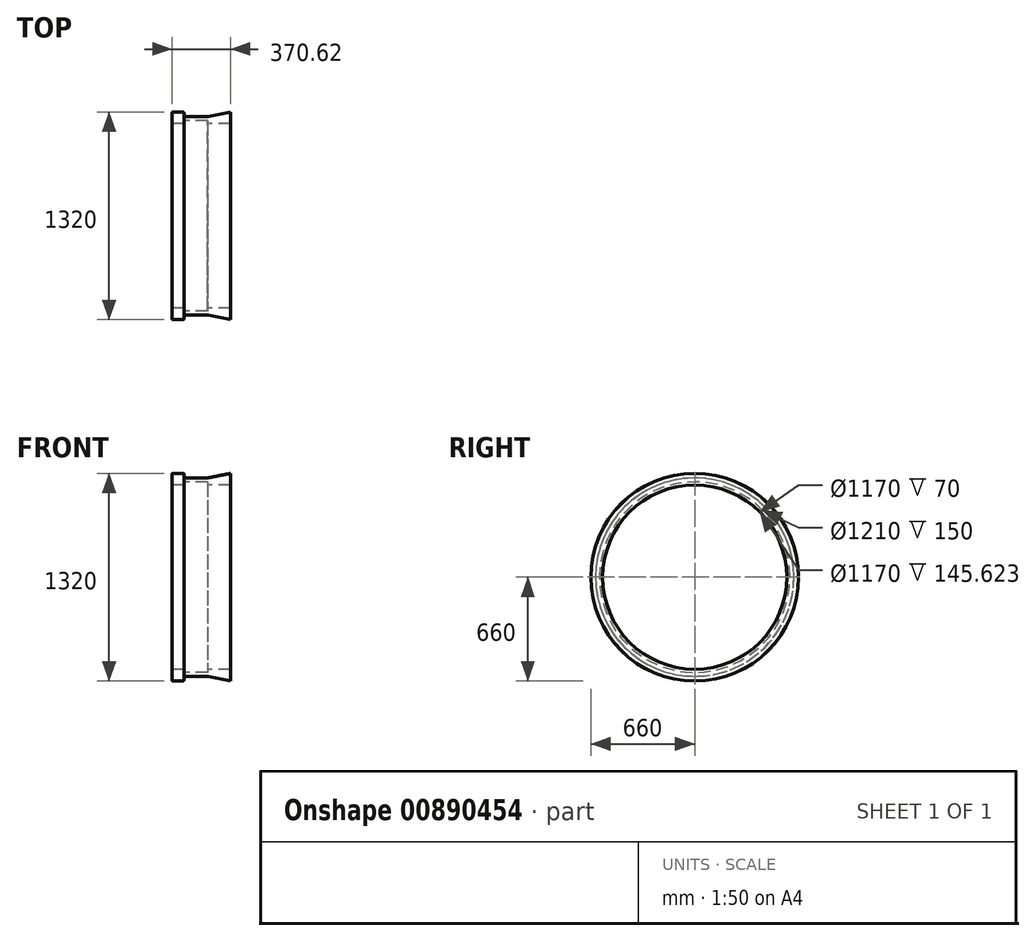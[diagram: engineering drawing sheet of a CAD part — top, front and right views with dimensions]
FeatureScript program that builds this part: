
annotation { "Feature Type Name" : "Feature", "Feature Type Description" : "" }
export const myFeature = defineFeature(function(context is Context, id is Id, definition is map)
    precondition{}
    {
        {
            var Q0;
            Q0=qCreatedBy(makeId("Front.planeOp"),FACE);
            var sketch = newSketch(context, id + "F0", { "sketchPlane" : qUnion([Q0])});
            skLineSegment(sketch, "E0", {"start": v(0, 660) * mm, "end": v(0, 585) * mm});
            skLineSegment(sketch, "E1", {"start": v(0, 0) * mm, "end": v(36.17, 0) * mm, "construction": true});
            skLineSegment(sketch, "E2", {"start": v(0, 585) * mm, "end": v(75, 585) * mm});
            skLineSegment(sketch, "E3", {"start": v(500, 685) * mm, "end": v(1070, 685) * mm});
            skLineSegment(sketch, "E4", {"start": v(1070, 685) * mm, "end": v(1070, 585) * mm});
            skLineSegment(sketch, "E5", {"start": v(0, 660) * mm, "end": v(75, 660) * mm});
            skLineSegment(sketch, "E6", {"start": v(75, 660) * mm, "end": v(75, 630) * mm});
            skLineSegment(sketch, "E7", {"start": v(75, 630) * mm, "end": v(75, 630) * mm});
            skLineSegment(sketch, "E8", {"start": v(75, 630) * mm, "end": v(225, 630) * mm});
            skLineSegment(sketch, "E9", {"start": v(225, 630) * mm, "end": v(225, 630) * mm});
            skLineSegment(sketch, "E10", {"start": v(500, 685) * mm, "end": v(225, 630) * mm});
            skLineSegment(sketch, "E11", {"start": v(75, 585) * mm, "end": v(75, 605) * mm});
            skLineSegment(sketch, "E12", {"start": v(75, 605) * mm, "end": v(225, 605) * mm});
            skLineSegment(sketch, "E13", {"start": v(225, 605) * mm, "end": v(225, 585) * mm});
            skLineSegment(sketch, "E14.trimOffspring", {"start": v(225, 585) * mm, "end": v(1070, 585) * mm});
            skSolve(sketch);
        }
        {
            var Q0;
            Q0=qCreatedBy(makeId("Front.planeOp"),FACE);
            var sketch = newSketch(context, id + "F1", { "sketchPlane" : qUnion([Q0])});
            skLineSegment(sketch, "E15", {"start": v(0, 0) * mm, "end": v(777.1, 0) * mm, "construction": true});
            skSolve(sketch);
        }
        {
            var Q0;
            Q0=makeQuery(id+"F0.imprint","IMPRINT",FACE,{"disambiguationData":[TD([[makeQuery(id+"F0.imprint","IMPRINT",EDGE,{"derivedFrom":sQuery(id+"F0.wireOp",EDGE,"E0")}),1.0]])]});
            var Q1;
            Q1=sQuery(id+"F1.wireOp",EDGE,"E15");
            revolve(context, id + "F2", {"surfaceOperationType" : NewSurfaceOperationType.NEW, "entities" : qUnion([Q0]), "axis" : qUnion([Q1]), "revolveType" : RevolveType.FULL});
        }
        {
            var Q0;
            Q0=makeQuery(id+"F2.opRevolve","SWEPT_EDGE",EDGE,{"disambiguationData":[OSD([sQuery(id+"F0.wireOp",EDGE,"E3"),sQuery(id+"F0.wireOp",EDGE,"E10")])]});
            var Q1;
            Q1=makeQuery(id+"F2.opRevolve","SWEPT_EDGE",EDGE,{"disambiguationData":[OSD([sQuery(id+"F0.wireOp",EDGE,"E8"),sQuery(id+"F0.wireOp",EDGE,"E10")])]});
            fillet(context, id + "F3", {"entities" : qUnion([Q0, Q1]), "radius" : 50 * mm, "tangentPropagation" : true, "allowEdgeOverflow" : false});
        }
        {
            var Q0;
            Q0=makeQuery(id+"F2.opRevolve","SWEPT_EDGE",EDGE,{"disambiguationData":[OSD([sQuery(id+"F0.wireOp",EDGE,"E5"),sQuery(id+"F0.wireOp",EDGE,"E6")])]});
            var Q1;
            Q1=makeQuery(id+"F2.opRevolve","SWEPT_EDGE",EDGE,{"disambiguationData":[OSD([sQuery(id+"F0.wireOp",EDGE,"E6"),sQuery(id+"F0.wireOp",EDGE,"E8")])]});
            var Q2;
            Q2=makeQuery(id+"F2.opRevolve","SWEPT_EDGE",EDGE,{"disambiguationData":[OSD([sQuery(id+"F0.wireOp",EDGE,"E0"),sQuery(id+"F0.wireOp",EDGE,"E5")])]});
            var Q3;
            Q3=makeQuery(id+"F2.opRevolve","SWEPT_FACE",FACE,{"disambiguationData":[OSD([sQuery(id+"F0.wireOp",EDGE,"E0")])]});
            var Q4;
            Q4=makeQuery(id+"F2.opRevolve","SWEPT_EDGE",EDGE,{"disambiguationData":[OSD([sQuery(id+"F0.wireOp",EDGE,"E3"),sQuery(id+"F0.wireOp",EDGE,"E4")])]});
            fillet(context, id + "F4", {"entities" : qUnion([Q0, Q1, Q2, Q3, Q4]), "radius" : 5 * mm, "tangentPropagation" : true, "allowEdgeOverflow" : false});
        }
        {
            var Q0;
            Q0=qCreatedBy(makeId("Front.planeOp"),FACE);
            var sketch = newSketch(context, id + "F5", { "sketchPlane" : qUnion([Q0])});
            skLineSegment(sketch, "E16.bottom", {"start": v(370.62, 876.98) * mm, "end": v(1277.49, 876.98) * mm});
            skLineSegment(sketch, "E16.top", {"start": v(370.62, -867.76) * mm, "end": v(1277.49, -867.76) * mm});
            skLineSegment(sketch, "E16.left", {"start": v(370.62, 876.98) * mm, "end": v(370.62, -867.76) * mm});
            skLineSegment(sketch, "E16.right", {"start": v(1277.49, 876.98) * mm, "end": v(1277.49, -867.76) * mm});
            skSolve(sketch);
        }
        {
            var Q0;
            Q0 = qSketchRegion(id + "F5", true);
            extrude(context, id + "F6", {"entities" : qUnion([Q0]), "operationType" : NewBodyOperationType.REMOVE, "endBound" : BoundingType.SYMMETRIC, "oppositeDirection" : true, "depth" : 2000 * mm, "offsetDistance" : 25 * mm});
        }
    });
